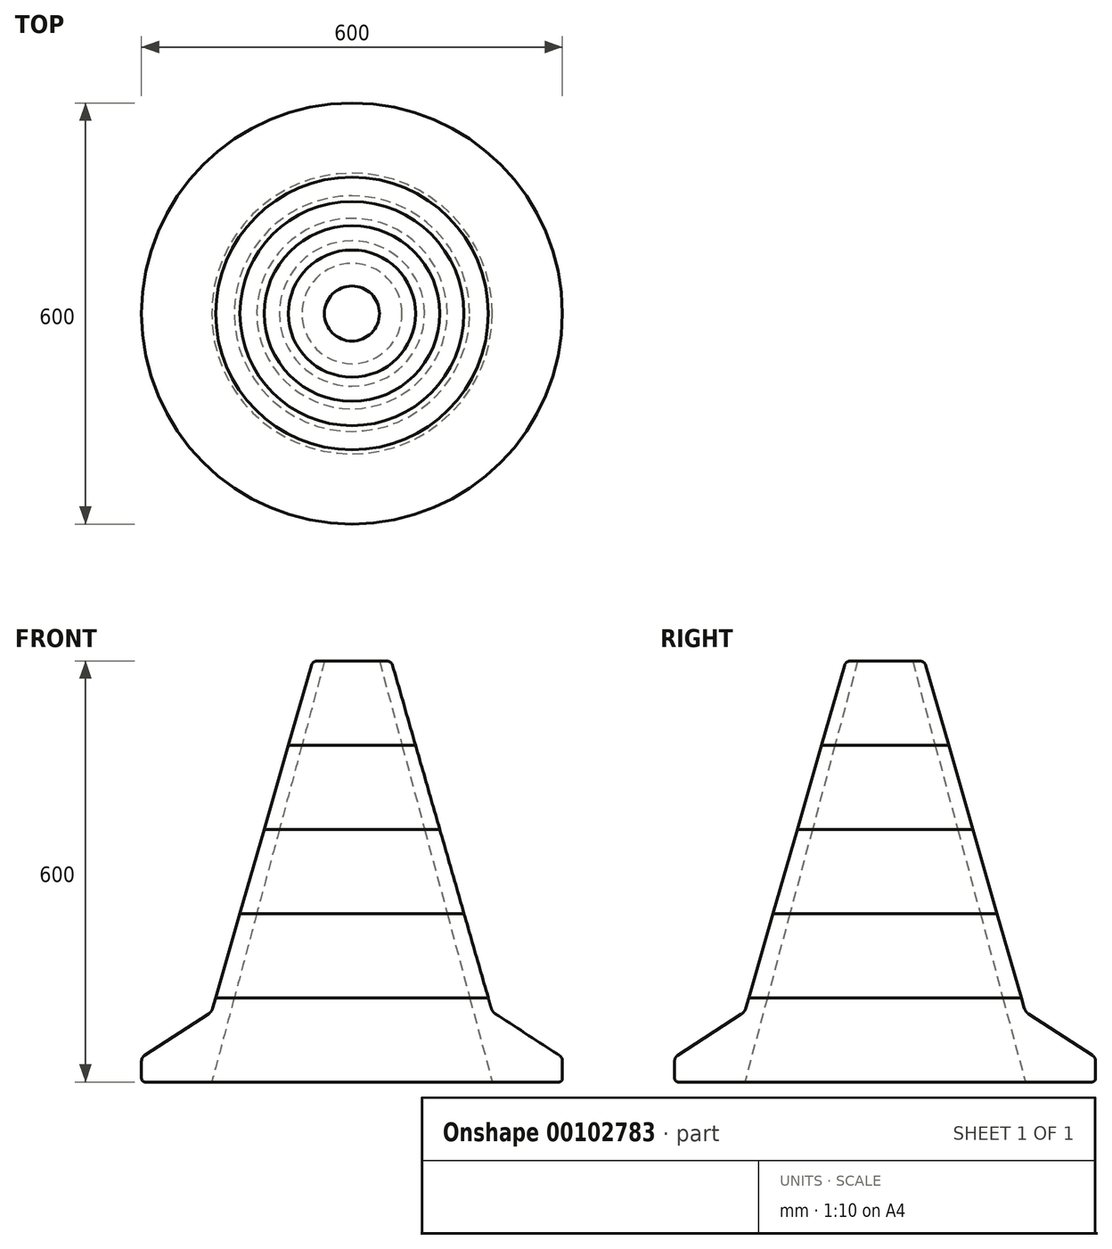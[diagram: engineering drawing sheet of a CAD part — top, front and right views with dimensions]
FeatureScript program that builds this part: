
annotation { "Feature Type Name" : "Feature", "Feature Type Description" : "" }
export const myFeature = defineFeature(function(context is Context, id is Id, definition is map)
    precondition{}
    {
        {
            var Q0;
            Q0=qCreatedBy(makeId("Front.planeOp"),FACE);
            var sketch = newSketch(context, id + "F0", { "sketchPlane" : qUnion([Q0])});
            skLineSegment(sketch, "E0", {"start": v(0, 0) * mm, "end": v(-295, 0) * mm});
            skLineSegment(sketch, "E1", {"start": v(-198.45, 105.38) * mm, "end": v(-57.94, 593.49) * mm});
            skLineSegment(sketch, "E2", {"start": v(-49.3, 600) * mm, "end": v(0, 600) * mm});
            skLineSegment(sketch, "E3", {"start": v(0, 600) * mm, "end": v(0, 0) * mm});
            skLineSegment(sketch, "E4", {"start": v(-90.61, 480) * mm, "end": v(0, 480) * mm});
            skLineSegment(sketch, "E5", {"start": v(-125.16, 360) * mm, "end": v(0, 360) * mm});
            skLineSegment(sketch, "E6", {"start": v(-159.7, 240) * mm, "end": v(0, 240) * mm});
            skLineSegment(sketch, "E7", {"start": v(-194.24, 120) * mm, "end": v(0, 120) * mm});
            skLineSegment(sketch, "E8", {"start": v(-300, 5) * mm, "end": v(-300, 30.12) * mm});
            skLineSegment(sketch, "E9", {"start": v(-295.9, 37.66) * mm, "end": v(-204.7, 96.95) * mm});
            skPoint(sketch, "E10.visualSharp", {"position": v(-300, 35) * mm});
            skArc(sketch, "E10.filletArc", {"start": v(-295.9, 37.66) * mm, "mid": v(-298.91, 34.4) * mm, "end": v(-300, 30.12) * mm});
            skPoint(sketch, "E11.visualSharp", {"position": v(-200, 100) * mm});
            skArc(sketch, "E11.filletArc", {"start": v(-204.7, 96.95) * mm, "mid": v(-200.81, 100.6) * mm, "end": v(-198.45, 105.38) * mm});
            skPoint(sketch, "E12.visualSharp", {"position": v(-300, 0) * mm});
            skArc(sketch, "E12.filletArc", {"start": v(-300, 5) * mm, "mid": v(-298.54, 1.46) * mm, "end": v(-295, 0) * mm});
            skPoint(sketch, "E13.visualSharp", {"position": v(-56.07, 600) * mm});
            skArc(sketch, "E13.filletArc", {"start": v(-49.3, 600) * mm, "mid": v(-54.7, 598.2) * mm, "end": v(-57.94, 593.49) * mm});
            skSolve(sketch);
        }
        {
            var Q0;
            {var subQ0=sQuery(id+"F0.wireOp",EDGE,"E2");Q0=makeQuery(id+"F0.imprint","IMPRINT",FACE,{"disambiguationData":[TD([[makeQuery(id+"F0.imprint","IMPRINT",EDGE,{"derivedFrom":subQ0}),-1.0]])]});}
            var Q1;
            Q1=sQuery(id+"F0.wireOp",EDGE,"E3");
            revolve(context, id + "F1", {"entities" : qUnion([Q0]), "axis" : qUnion([Q1]), "revolveType" : RevolveType.FULL});
        }
        {
            var Q0;
            {var subQ0=sQuery(id+"F0.wireOp",EDGE,"E4");Q0=makeQuery(id+"F0.imprint","IMPRINT",FACE,{"disambiguationData":[TD([[makeQuery(id+"F0.imprint","IMPRINT",EDGE,{"derivedFrom":subQ0}),-1.0]])]});}
            var Q1;
            Q1=sQuery(id+"F0.wireOp",EDGE,"E3");
            revolve(context, id + "F2", {"entities" : qUnion([Q0]), "axis" : qUnion([Q1]), "revolveType" : RevolveType.FULL});
        }
        {
            var Q0;
            {var subQ0=sQuery(id+"F0.wireOp",EDGE,"E5");Q0=makeQuery(id+"F0.imprint","IMPRINT",FACE,{"disambiguationData":[TD([[makeQuery(id+"F0.imprint","IMPRINT",EDGE,{"derivedFrom":subQ0}),-1.0]])]});}
            var Q1;
            Q1=sQuery(id+"F0.wireOp",EDGE,"E3");
            revolve(context, id + "F3", {"entities" : qUnion([Q0]), "axis" : qUnion([Q1]), "revolveType" : RevolveType.FULL});
        }
        {
            var Q0;
            {var subQ0=sQuery(id+"F0.wireOp",EDGE,"E6");Q0=makeQuery(id+"F0.imprint","IMPRINT",FACE,{"disambiguationData":[TD([[makeQuery(id+"F0.imprint","IMPRINT",EDGE,{"derivedFrom":subQ0}),-1.0]])]});}
            var Q1;
            Q1=sQuery(id+"F0.wireOp",EDGE,"E3");
            revolve(context, id + "F4", {"entities" : qUnion([Q0]), "axis" : qUnion([Q1]), "revolveType" : RevolveType.FULL});
        }
        {
            var Q0;
            {var subQ3=sQuery(id+"F0.wireOp",EDGE,"E0");Q0=makeQuery(id+"F0.imprint","IMPRINT",FACE,{"disambiguationData":[TD([[makeQuery(id+"F0.imprint","IMPRINT",EDGE,{"derivedFrom":subQ3}),-1.0]])]});}
            var Q1;
            Q1=sQuery(id+"F0.wireOp",EDGE,"E3");
            revolve(context, id + "F5", {"entities" : qUnion([Q0]), "axis" : qUnion([Q1]), "revolveType" : RevolveType.FULL});
        }
        {
            var Q0;
            Q0=makeQuery(id+"F5.opRevolve","SWEPT_FACE",FACE,{"disambiguationData":[OSD([sQuery(id+"F0.wireOp",EDGE,"E0")])]});
            var sketch = newSketch(context, id + "F6", { "sketchPlane" : qUnion([Q0])});
            skCircle(sketch, "E14", {"center": v(0, 0) * mm, "radius": 200 * mm});
            skSolve(sketch);
        }
        {
            var Q0;
            Q0=makeQuery(id+"F6.imprint","IMPRINT",FACE,{"disambiguationData":[TD([[makeQuery(id+"F6.imprint","IMPRINT",EDGE,{"derivedFrom":sQuery(id+"F6.wireOp",EDGE,"E14")}),1.0]])]});
            extrude(context, id + "F7", {"entities" : qUnion([Q0]), "operationType" : NewBodyOperationType.REMOVE, "endBound" : BoundingType.THROUGH_ALL, "oppositeDirection" : true, "depth" : 25 * mm, "hasDraft" : true, "draftAngle" : 15 * degree, "draftPullDirection" : true});
        }
    });
